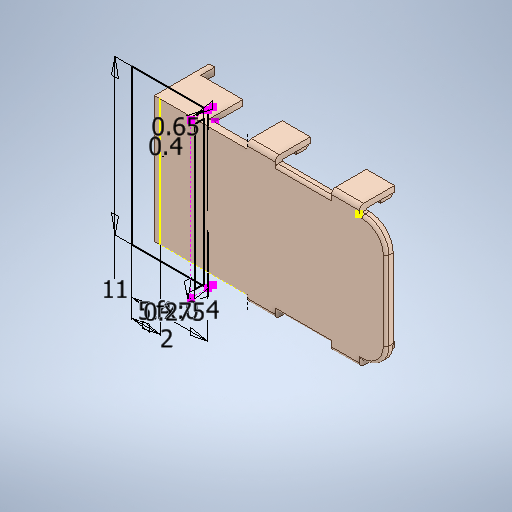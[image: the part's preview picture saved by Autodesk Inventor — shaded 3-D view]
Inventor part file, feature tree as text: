
AUTODESK INVENTOR PART (.ipt)
format: ipt  version: 2025 (Build 290162000, 162)  size: 484,864 bytes
history: native  units: in
note: dims shown in document units (in); Inventor stores cm internally (conversion verified against a paired STEP export)
features: reference x25, extrude x7, other x6, plane x3, fillet x3, sketch x2, chamfer x1, projected_geometry x1
ambient origin geometry x8: Origin, YZ Plane, XZ Plane, XY Plane, X Axis, Y Axis, Z Axis, Center Point
bodies: Solid1 (feature_tree)
feature tree (48):
  plane  "Work Plane1"
  extrude  "main"  Depth=0.0787in TaperAngle=0.0deg
  extrude  "flaps"  Depth=0.0197in
  extrude  "Extrusion18"  Depth=0.0079in
  plane  "Work Plane4"
  extrude  "Extrusion19"  Depth=0.0039in
  fillet  "Fillet7"  Radius=0.0039in
  fillet  "Fillet9"  Radius=0.0039in
  extrude  "Extrusion22"  Depth=0.0039in
  extrude  "Extrusion23"  Depth=0.0079in
  chamfer  "Chamfer6"  Distance=0.0945in
  fillet  "Fillet11"  Radius=0.0157in
  plane  "Work Plane3"
  extrude  "Extrusion24"  Depth=0.0197in
  reference  "Reference10"
  reference  "Reference11"
  reference  "Reference31"
  reference  "Reference32"
  reference  "Reference33"
  reference  "Reference34"
  reference  "Reference35"
  reference  "Reference36"
  reference  "Reference37"
  reference  "Reference38"
  reference  "Reference39"
  reference  "Reference40"
  reference  "Reference41"
  reference  "Reference42"
  reference  "Reference43"
  reference  "Reference44"
  reference  "Reference45"
  sketch  "Sketch19"  dims[d2=0.0197in d3=0.0in d6=0.0787in d7=0.0in]
  reference  "Reference49"
  reference  "Reference50"
  reference  "Reference51"
  reference  "Reference52"
  reference  "Reference53"
  reference  "Reference54"
  reference  "Reference55"
  reference  "Reference56"
  sketch  "Sketch24"  dims[d50=0.0157in d89=0.0197in d90=0.0079in d91=0.0039in d92=0.0039in d93=0.0039in d94=0.0039in d95=0.0079in d96=0.0945in d97=0.0in d98=0.0157in d99=0.0in d100=0.2126in d101=0.4331in d102=0.0787in d105=0.0108in d106=0.0256in d107=0.0157in d108=0.0157in d120=0.0118in d125=0.0079in d126=0.0669in d134=0.0039in d135=0.0079in d136=0.0039in d137=0.0039in d138=0.0039in d139=0.0039in d140=0.0039in d141=0.0118in d142=0.0in d143=0.0118in d144=0.0in d145=0.0079in d146=0.0591in d147=45.0deg d151=0.0079in d152=0.315in d153=0.0197in d154=0.0197in d155=0.3937in d156=0.0in d38=0.0in d39=0.0in d40=0.0in d41=0.0in d61=0.0in d62=0.0in d63=0.0in d64=0.0in d83=0.0197in d84=0.0344in d85=0.0197in d86=0.0344in d121=0.0in d122=0.0in d123=0.0in]
  projected_geometry  "Projected Loop2"
  parser-record x2  (decoder bookkeeping rows leaked as tree rows — omitted from the tree; the rows remain in map.json)
  other  "np2alpha_full_assembly.iam"
  other  "np2alpha_main_chassis:1"
  other  "np2a_assembly.iam"
  other  "np2a:1"
note: 2 file-system paths scrubbed to <path> (originals preserved in map.json)
